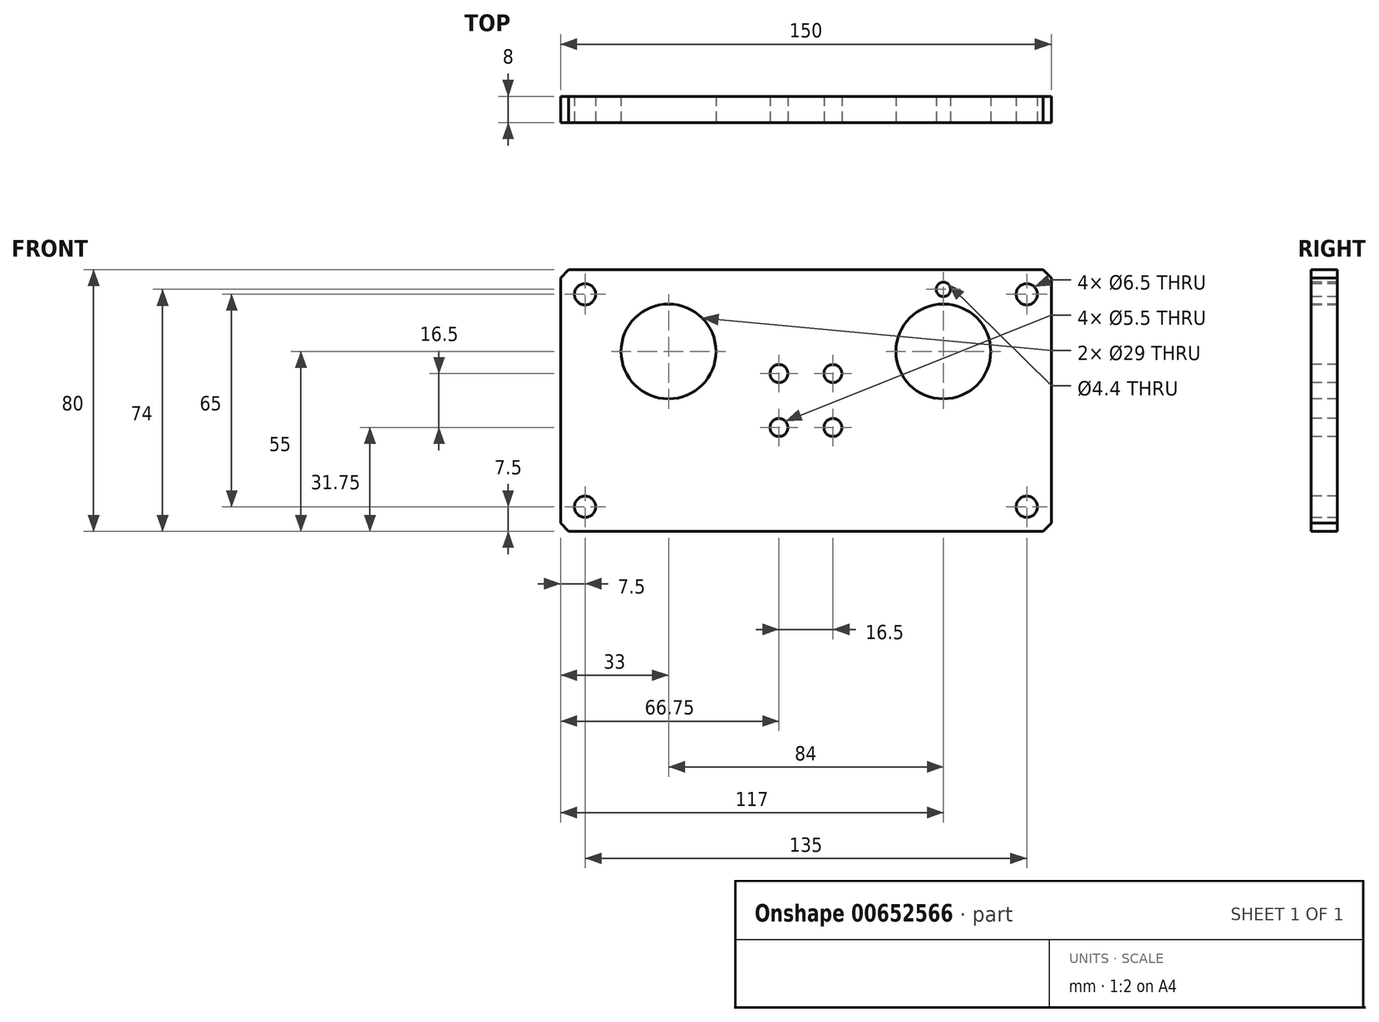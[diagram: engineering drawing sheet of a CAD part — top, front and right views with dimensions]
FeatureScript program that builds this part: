
annotation { "Feature Type Name" : "Feature", "Feature Type Description" : "" }
export const myFeature = defineFeature(function(context is Context, id is Id, definition is map)
    precondition{}
    {
        {
            var Q0;
            Q0=qCreatedBy(makeId("Front.planeOp"),FACE);
            var sketch = newSketch(context, id + "F0", { "sketchPlane" : qUnion([Q0])});
            skLineSegment(sketch, "E0.bottom", {"start": v(75, -40) * mm, "end": v(-75, -40) * mm});
            skLineSegment(sketch, "E0.top", {"start": v(75, 40) * mm, "end": v(-75, 40) * mm});
            skLineSegment(sketch, "E0.left", {"start": v(75, -40) * mm, "end": v(75, 40) * mm});
            skLineSegment(sketch, "E0.right", {"start": v(-75, -40) * mm, "end": v(-75, 40) * mm});
            skPoint(sketch, "E0.middle", {"position": v(0, 0) * mm});
            skSolve(sketch);
        }
        {
            var Q0;
            Q0=makeQuery(id+"F0.imprint","IMPRINT",FACE,{"disambiguationData":[TD([[makeQuery(id+"F0.imprint","IMPRINT",EDGE,{"derivedFrom":sQuery(id+"F0.wireOp",EDGE,"E0.bottom")}),-1.0]])]});
            extrude(context, id + "F1", {"entities" : qUnion([Q0]), "depth" : 8 * mm, "offsetDistance" : 25 * mm});
        }
        {
            var Q0;
            Q0=makeQuery(id+"F1.opExtrude","SWEPT_EDGE",EDGE,{"disambiguationData":[OSD([sQuery(id+"F0.wireOp",EDGE,"E0.top"),sQuery(id+"F0.wireOp",EDGE,"E0.left")])]});
            var Q1;
            Q1=makeQuery(id+"F1.opExtrude","SWEPT_EDGE",EDGE,{"disambiguationData":[OSD([sQuery(id+"F0.wireOp",EDGE,"E0.bottom"),sQuery(id+"F0.wireOp",EDGE,"E0.left")])]});
            var Q2;
            Q2=makeQuery(id+"F1.opExtrude","SWEPT_EDGE",EDGE,{"disambiguationData":[OSD([sQuery(id+"F0.wireOp",EDGE,"E0.top"),sQuery(id+"F0.wireOp",EDGE,"E0.right")])]});
            var Q3;
            Q3=makeQuery(id+"F1.opExtrude","SWEPT_EDGE",EDGE,{"disambiguationData":[OSD([sQuery(id+"F0.wireOp",EDGE,"E0.bottom"),sQuery(id+"F0.wireOp",EDGE,"E0.right")])]});
            chamfer(context, id + "F2", {"entities" : qUnion([Q0, Q1, Q2, Q3]), "width" : 2.5 * mm, "tangentPropagation" : true});
        }
        {
            var Q0;
            Q0=makeQuery(id+"F1.opExtrude","CAP_FACE",FACE,{"disambiguationData":[OSD([sQuery(id+"F0.wireOp",EDGE,"E0.bottom"),sQuery(id+"F0.wireOp",EDGE,"E0.top"),sQuery(id+"F0.wireOp",EDGE,"E0.left"),sQuery(id+"F0.wireOp",EDGE,"E0.right")])],"isStart":false});
            var sketch = newSketch(context, id + "F3", { "sketchPlane" : qUnion([Q0])});
            skPoint(sketch, "E1", {"position": v(0, 0) * mm});
            skPoint(sketch, "E2", {"position": v(-42, 15) * mm});
            skPoint(sketch, "E3", {"position": v(42, 15) * mm});
            skPoint(sketch, "E4", {"position": v(-67.5, 32.5) * mm});
            skPoint(sketch, "E5", {"position": v(-67.5, -32.5) * mm});
            skPoint(sketch, "E6", {"position": v(67.5, -32.5) * mm});
            skPoint(sketch, "E7", {"position": v(67.5, 32.5) * mm});
            skPoint(sketch, "E8", {"position": v(42, 34) * mm});
            skPoint(sketch, "E9", {"position": v(-8.25, 8.25) * mm});
            skPoint(sketch, "E10", {"position": v(8.25, 8.25) * mm});
            skPoint(sketch, "E11", {"position": v(-8.25, -8.25) * mm});
            skPoint(sketch, "E12", {"position": v(8.25, -8.25) * mm});
            skSolve(sketch);
        }
        {
            var Q0;
            Q0=sQuery(id+"F3.wireOp",VERTEX,"E8");
            var Q1;
            Q1=makeQuery(id+"F1.opExtrude","SWEPT_BODY",BODY,{"disambiguationData":[OSD([sQuery(id+"F0.wireOp",EDGE,"E0.bottom"),sQuery(id+"F0.wireOp",EDGE,"E0.top"),sQuery(id+"F0.wireOp",EDGE,"E0.left"),sQuery(id+"F0.wireOp",EDGE,"E0.right")])]});
            hole(context, id + "F4", {"style" : HoleStyle.SIMPLE, "endStyle" : HoleEndStyle.THROUGH, "standardTappedOrClearance" : lookupTablePath({ "standard" : "ISO", "fit" : "Normal", "size" : "M4", "type" : "Clearance" }), "standardBlindInLast" : lookupTablePath({ "fit" : "Standard", "standard" : "ISO", "size" : "M4", "type" : "Clearance" }), "holeDiameter" : 4.4 * mm, "majorDiameter" : 5 * mm, "isTappedThrough" : true, "tappedDepth" : 12 * mm, "tapClearance" : 3, "locations" : qUnion([Q0]), "scope" : qUnion([Q1])});
        }
        {
            var Q0;
            Q0=sQuery(id+"F3.wireOp",VERTEX,"E7");
            var Q1;
            Q1=sQuery(id+"F3.wireOp",VERTEX,"E6");
            var Q2;
            Q2=sQuery(id+"F3.wireOp",VERTEX,"E5");
            var Q3;
            Q3=sQuery(id+"F3.wireOp",VERTEX,"E4");
            var Q4;
            Q4=makeQuery(id+"F1.opExtrude","SWEPT_BODY",BODY,{"disambiguationData":[OSD([sQuery(id+"F0.wireOp",EDGE,"E0.bottom"),sQuery(id+"F0.wireOp",EDGE,"E0.top"),sQuery(id+"F0.wireOp",EDGE,"E0.left"),sQuery(id+"F0.wireOp",EDGE,"E0.right")])]});
            hole(context, id + "F5", {"style" : HoleStyle.SIMPLE, "endStyle" : HoleEndStyle.THROUGH, "holeDiameter" : 6.5 * mm, "majorDiameter" : 5 * mm, "isTappedThrough" : true, "tappedDepth" : 12 * mm, "tapClearance" : 3, "locations" : qUnion([Q0, Q1, Q2, Q3]), "scope" : qUnion([Q4])});
        }
        {
            var Q0;
            Q0=sQuery(id+"F3.wireOp",VERTEX,"E11");
            var Q1;
            Q1=sQuery(id+"F3.wireOp",VERTEX,"E12");
            var Q2;
            Q2=sQuery(id+"F3.wireOp",VERTEX,"E10");
            var Q3;
            Q3=sQuery(id+"F3.wireOp",VERTEX,"E9");
            var Q4;
            Q4=makeQuery(id+"F1.opExtrude","SWEPT_BODY",BODY,{"disambiguationData":[OSD([sQuery(id+"F0.wireOp",EDGE,"E0.bottom"),sQuery(id+"F0.wireOp",EDGE,"E0.top"),sQuery(id+"F0.wireOp",EDGE,"E0.left"),sQuery(id+"F0.wireOp",EDGE,"E0.right")])]});
            hole(context, id + "F6", {"style" : HoleStyle.SIMPLE, "endStyle" : HoleEndStyle.THROUGH, "holeDiameter" : 5.5 * mm, "majorDiameter" : 5 * mm, "isTappedThrough" : true, "tappedDepth" : 12 * mm, "tapClearance" : 3, "locations" : qUnion([Q0, Q1, Q2, Q3]), "scope" : qUnion([Q4])});
        }
        {
            var Q0;
            Q0=sQuery(id+"F3.wireOp",VERTEX,"E2");
            var Q1;
            Q1=sQuery(id+"F3.wireOp",VERTEX,"E3");
            var Q2;
            Q2=makeQuery(id+"F1.opExtrude","SWEPT_BODY",BODY,{"disambiguationData":[OSD([sQuery(id+"F0.wireOp",EDGE,"E0.bottom"),sQuery(id+"F0.wireOp",EDGE,"E0.top"),sQuery(id+"F0.wireOp",EDGE,"E0.left"),sQuery(id+"F0.wireOp",EDGE,"E0.right")])]});
            hole(context, id + "F7", {"style" : HoleStyle.SIMPLE, "endStyle" : HoleEndStyle.THROUGH, "holeDiameter" : 29 * mm, "majorDiameter" : 5 * mm, "isTappedThrough" : true, "tappedDepth" : 12 * mm, "tapClearance" : 3, "locations" : qUnion([Q0, Q1]), "scope" : qUnion([Q2])});
        }
    });
